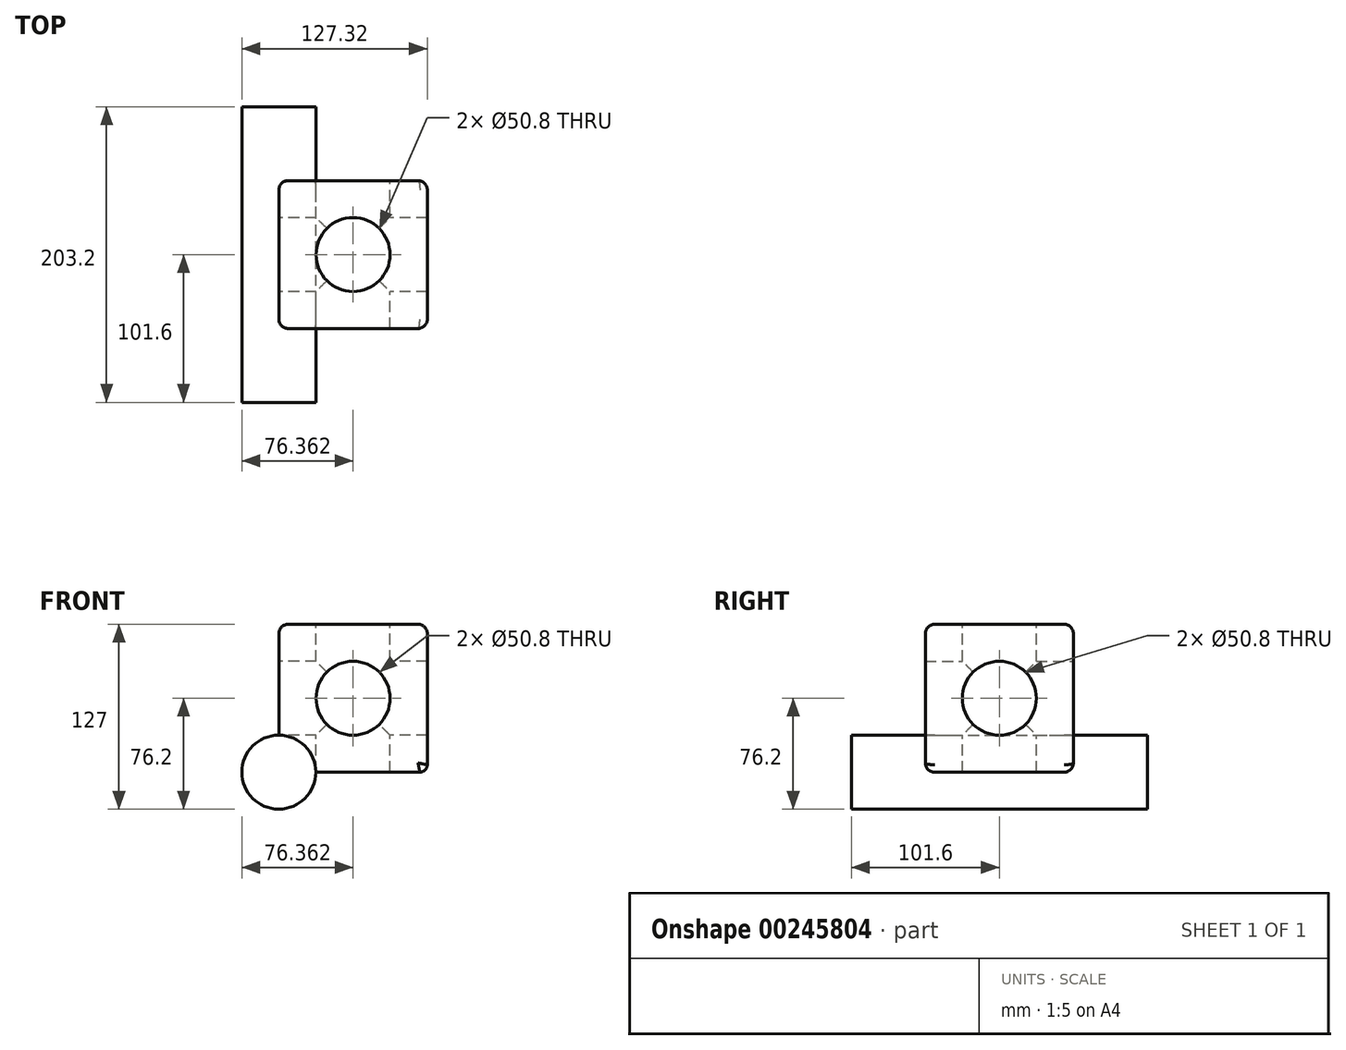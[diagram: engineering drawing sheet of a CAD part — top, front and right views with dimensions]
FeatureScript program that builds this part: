
annotation { "Feature Type Name" : "Feature", "Feature Type Description" : "" }
export const myFeature = defineFeature(function(context is Context, id is Id, definition is map)
    precondition{}
    {
        {
            var Q0;
            Q0=qCreatedBy(makeId("Front.planeOp"),FACE);
            var sketch = newSketch(context, id + "F0", { "sketchPlane" : qUnion([Q0])});
            skLineSegment(sketch, "E0", {"start": v(0, 0) * mm, "end": v(101.92, 0) * mm});
            skLineSegment(sketch, "E1", {"start": v(0, 0) * mm, "end": v(0, 101.6) * mm});
            skLineSegment(sketch, "E2", {"start": v(0, 101.6) * mm, "end": v(101.92, 101.6) * mm});
            skLineSegment(sketch, "E3", {"start": v(101.92, 101.6) * mm, "end": v(101.92, 0) * mm});
            skSolve(sketch);
        }
        {
            var Q0;
            Q0=makeQuery(id+"F0.imprint","IMPRINT",FACE,{"disambiguationData":[TD([[makeQuery(id+"F0.imprint","IMPRINT",EDGE,{"derivedFrom":sQuery(id+"F0.wireOp",EDGE,"E0")}),1.0]])]});
            extrude(context, id + "F1", {"entities" : qUnion([Q0]), "depth" : 101.6 * mm});
        }
        {
            var Q0;
            Q0=makeQuery(id+"F1.opExtrude","SWEPT_FACE",FACE,{"disambiguationData":[OSD([sQuery(id+"F0.wireOp",EDGE,"E2")])]});
            var sketch = newSketch(context, id + "F2", { "sketchPlane" : qUnion([Q0])});
            skLineSegment(sketch, "E4", {"start": v(50.96, 0) * mm, "end": v(50.96, -101.6) * mm});
            skCircle(sketch, "E5", {"center": v(50.96, -50.8) * mm, "radius": 25.4 * mm});
            skSolve(sketch);
        }
        {
            var Q0;
            {var subQ0=sQuery(id+"F2.wireOp",EDGE,"E5");var subQ1=sQuery(id+"F2.wireOp",EDGE,"E4");var subQ2=makeQuery(id+"F2.imprint","INTERSECT",VERTEX,{"disambiguationData":[OD(0.0)],"derivedFrom":[subQ1,subQ0]});Q0=makeQuery(id+"F2.imprint","IMPRINT",FACE,{"disambiguationData":[TD([[makeQuery(id+"F2.imprint","IMPRINT",EDGE,{"disambiguationData":[TD([[subQ2,-1.0]])],"derivedFrom":subQ1}),-1.0]])]});}
            var Q1;
            {var subQ0=sQuery(id+"F2.wireOp",EDGE,"E5");var subQ1=sQuery(id+"F2.wireOp",EDGE,"E4");var subQ2=makeQuery(id+"F2.imprint","INTERSECT",VERTEX,{"disambiguationData":[OD(0.0)],"derivedFrom":[subQ1,subQ0]});Q1=makeQuery(id+"F2.imprint","IMPRINT",FACE,{"disambiguationData":[TD([[makeQuery(id+"F2.imprint","IMPRINT",EDGE,{"disambiguationData":[TD([[subQ2,-1.0]])],"derivedFrom":subQ1}),1.0]])]});}
            extrude(context, id + "F3", {"entities" : qUnion([Q0, Q1]), "operationType" : NewBodyOperationType.REMOVE, "oppositeDirection" : true, "depth" : 101.6 * mm});
        }
        {
            var Q0;
            Q0=makeQuery(id+"F1.opExtrude","SWEPT_FACE",FACE,{"disambiguationData":[OSD([sQuery(id+"F0.wireOp",EDGE,"E1")])]});
            var sketch = newSketch(context, id + "F4", { "sketchPlane" : qUnion([Q0])});
            skLineSegment(sketch, "E6", {"start": v(50.8, 101.6) * mm, "end": v(50.8, 0) * mm});
            skCircle(sketch, "E7", {"center": v(50.8, 50.8) * mm, "radius": 25.4 * mm});
            skSolve(sketch);
        }
        {
            var Q0;
            {var subQ0=sQuery(id+"F4.wireOp",EDGE,"E7");var subQ1=sQuery(id+"F4.wireOp",EDGE,"E6");var subQ2=makeQuery(id+"F4.imprint","INTERSECT",VERTEX,{"disambiguationData":[OD(0.0)],"derivedFrom":[subQ1,subQ0]});Q0=makeQuery(id+"F4.imprint","IMPRINT",FACE,{"disambiguationData":[TD([[makeQuery(id+"F4.imprint","IMPRINT",EDGE,{"disambiguationData":[TD([[subQ2,-1.0]])],"derivedFrom":subQ1}),-1.0]])]});}
            var Q1;
            {var subQ0=sQuery(id+"F4.wireOp",EDGE,"E7");var subQ1=sQuery(id+"F4.wireOp",EDGE,"E6");var subQ2=makeQuery(id+"F4.imprint","INTERSECT",VERTEX,{"disambiguationData":[OD(0.0)],"derivedFrom":[subQ1,subQ0]});Q1=makeQuery(id+"F4.imprint","IMPRINT",FACE,{"disambiguationData":[TD([[makeQuery(id+"F4.imprint","IMPRINT",EDGE,{"disambiguationData":[TD([[subQ2,-1.0]])],"derivedFrom":subQ1}),1.0]])]});}
            extrude(context, id + "F5", {"entities" : qUnion([Q0, Q1]), "operationType" : NewBodyOperationType.REMOVE, "oppositeDirection" : true, "depth" : 101.6 * mm});
        }
        {
            var Q0;
            Q0=makeQuery(id+"F5.boolean.opBoolean","COPY",FACE,{"derivedFrom":makeQuery(id+"F5.opExtrude","CAP_FACE",FACE,{"disambiguationData":[OSD([sQuery(id+"F4.wireOp",EDGE,"E7")])],"isStart":false})});
            extrude(context, id + "F6", {"entities" : qUnion([Q0]), "operationType" : NewBodyOperationType.REMOVE, "oppositeDirection" : true, "depth" : 101.6 * mm});
        }
        {
            var Q0;
            Q0=makeQuery(id+"F1.opExtrude","CAP_FACE",FACE,{"disambiguationData":[OSD([sQuery(id+"F0.wireOp",EDGE,"E0"),sQuery(id+"F0.wireOp",EDGE,"E1"),sQuery(id+"F0.wireOp",EDGE,"E2"),sQuery(id+"F0.wireOp",EDGE,"E3")])],"isStart":true});
            var sketch = newSketch(context, id + "F7", { "sketchPlane" : qUnion([Q0])});
            skLineSegment(sketch, "E8", {"start": v(-101.92, 50.8) * mm, "end": v(0, 50.8) * mm});
            skLineSegment(sketch, "E9", {"start": v(0, 50.8) * mm, "end": v(-101.92, 50.8) * mm});
            skCircle(sketch, "E10", {"center": v(-50.96, 50.8) * mm, "radius": 25.4 * mm});
            skSolve(sketch);
        }
        {
            var Q0;
            Q0 = qSketchRegion(id + "F7", true);
            extrude(context, id + "F8", {"entities" : qUnion([Q0]), "operationType" : NewBodyOperationType.REMOVE, "oppositeDirection" : true, "depth" : 101.6 * mm});
        }
        {
            var Q0;
            Q0=makeQuery(id+"F1.opExtrude","CAP_EDGE",EDGE,{"disambiguationData":[OSD([sQuery(id+"F0.wireOp",EDGE,"E0")])],"isStart":false});
            var Q1;
            Q1=makeQuery(id+"F1.opExtrude","CAP_EDGE",EDGE,{"disambiguationData":[OSD([sQuery(id+"F0.wireOp",EDGE,"E1")])],"isStart":false});
            var Q2;
            Q2=makeQuery(id+"F1.opExtrude","CAP_EDGE",EDGE,{"disambiguationData":[OSD([sQuery(id+"F0.wireOp",EDGE,"E2")])],"isStart":false});
            var Q3;
            Q3=makeQuery(id+"F1.opExtrude","CAP_EDGE",EDGE,{"disambiguationData":[OSD([sQuery(id+"F0.wireOp",EDGE,"E3")])],"isStart":false});
            fillet(context, id + "F9", {"entities" : qUnion([Q0, Q1, Q2, Q3]), "radius" : 6.35 * mm, "tangentPropagation" : true, "allowEdgeOverflow" : false});
        }
        {
            var Q0;
            Q0=makeQuery(id+"F9.opFillet","BLEND_EDGE",EDGE,{"blendedFrom":[makeQuery(id+"F1.opExtrude","CAP_EDGE",EDGE,{"disambiguationData":[OSD([sQuery(id+"F0.wireOp",EDGE,"E1")])],"isStart":false}),makeQuery(id+"F1.opExtrude","CAP_EDGE",EDGE,{"disambiguationData":[OSD([sQuery(id+"F0.wireOp",EDGE,"E2")])],"isStart":false})],"blendedInto":[]});
            var Q1;
            Q1=makeQuery(id+"F1.opExtrude","SWEPT_EDGE",EDGE,{"disambiguationData":[OSD([sQuery(id+"F0.wireOp",EDGE,"E2"),sQuery(id+"F0.wireOp",EDGE,"E3")])]});
            var Q2;
            Q2=makeQuery(id+"F1.opExtrude","SWEPT_EDGE",EDGE,{"disambiguationData":[OSD([sQuery(id+"F0.wireOp",EDGE,"E0"),sQuery(id+"F0.wireOp",EDGE,"E1")])]});
            var Q3;
            Q3=makeQuery(id+"F1.opExtrude","CAP_EDGE",EDGE,{"disambiguationData":[OSD([sQuery(id+"F0.wireOp",EDGE,"E1")])],"isStart":true});
            var Q4;
            Q4=makeQuery(id+"F1.opExtrude","CAP_EDGE",EDGE,{"disambiguationData":[OSD([sQuery(id+"F0.wireOp",EDGE,"E2")])],"isStart":true});
            var Q5;
            Q5=makeQuery(id+"F1.opExtrude","CAP_EDGE",EDGE,{"disambiguationData":[OSD([sQuery(id+"F0.wireOp",EDGE,"E3")])],"isStart":true});
            var Q6;
            Q6=makeQuery(id+"F1.opExtrude","CAP_EDGE",EDGE,{"disambiguationData":[OSD([sQuery(id+"F0.wireOp",EDGE,"E0")])],"isStart":true});
            fillet(context, id + "F10", {"entities" : qUnion([Q0, Q1, Q2, Q3, Q4, Q5, Q6]), "radius" : 6.35 * mm, "tangentPropagation" : true, "allowEdgeOverflow" : false});
        }
        {
            var Q0;
            Q0=makeQuery(id+"F1.opExtrude","SWEPT_EDGE",EDGE,{"disambiguationData":[OSD([sQuery(id+"F0.wireOp",EDGE,"E0"),sQuery(id+"F0.wireOp",EDGE,"E3")])]});
            var Q1;
            Q1=makeQuery(id+"F9.opFillet","BLEND_FACE",FACE,{"disambiguationData":[OSD([sQuery(id+"F0.wireOp",EDGE,"E0")])]});
            fillet(context, id + "F11", {"entities" : qUnion([Q0, Q1]), "radius" : 5.08 * mm, "tangentPropagation" : true, "allowEdgeOverflow" : false});
        }
        {
            var Q0;
            Q0=qCreatedBy(makeId("Front.planeOp"),FACE);
            cPlane(context, id + "F12", {"entities" : qUnion([Q0]), "cplaneType" : CPlaneType.OFFSET, "offset" : 101.6 * mm, "width" : 152.4 * mm, "height" : 152.4 * mm});
        }
        {
            var Q0;
            Q0=qCreatedBy(id+"F12.planeOp",FACE);
            var sketch = newSketch(context, id + "F13", { "sketchPlane" : qUnion([Q0])});
            skCircle(sketch, "E11", {"center": v(0, 0) * mm, "radius": 25.4 * mm});
            skSolve(sketch);
        }
        {
            var Q0;
            Q0 = qSketchRegion(id + "F13", true);
            extrude(context, id + "F14", {"entities" : qUnion([Q0]), "operationType" : NewBodyOperationType.ADD, "depth" : 50.8 * mm, "hasSecondDirection" : true, "secondDirectionOppositeDirection" : true, "secondDirectionDepth" : 152.4 * mm});
        }
    });
